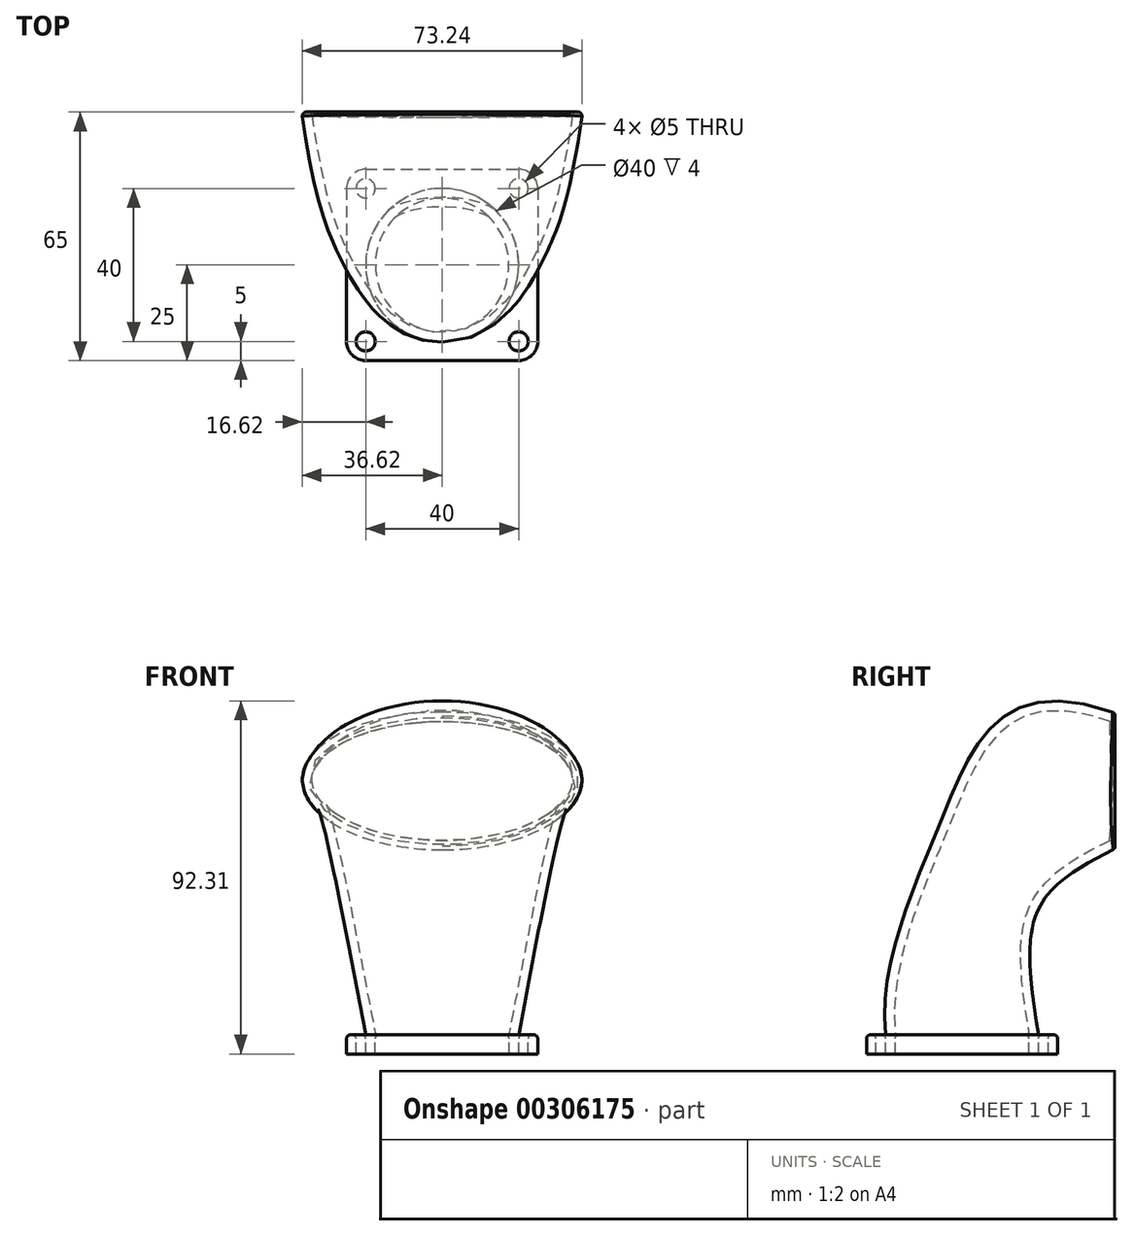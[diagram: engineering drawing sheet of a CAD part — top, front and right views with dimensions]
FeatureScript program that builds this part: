
annotation { "Feature Type Name" : "Feature", "Feature Type Description" : "" }
export const myFeature = defineFeature(function(context is Context, id is Id, definition is map)
    precondition{}
    {
        {
            var Q0;
            Q0=qCreatedBy(makeId("Top.planeOp"),FACE);
            var sketch = newSketch(context, id + "F0", { "sketchPlane" : qUnion([Q0])});
            skCircle(sketch, "E0", {"center": v(0, 0) * mm, "radius": 20 * mm});
            skSolve(sketch);
        }
        {
            var Q0;
            Q0=qCreatedBy(makeId("Front.planeOp"),FACE);
            cPlane(context, id + "F1", {"entities" : qUnion([Q0]), "cplaneType" : CPlaneType.OFFSET, "offset" : 40 * mm, "oppositeDirection" : true, "width" : 150 * mm, "height" : 150 * mm});
        }
        {
            var Q0;
            Q0=qCreatedBy(id+"F1.planeOp",FACE);
            var sketch = newSketch(context, id + "F2", { "sketchPlane" : qUnion([Q0])});
            skEllipse(sketch, "E1", {"center": v(0, 66.4) * mm, "majorRadius": 36.68 * mm, "minorRadius": 17.71 * mm, "majorAxis": v(-1, 0)});
            skSolve(sketch);
        }
        {
            var Q0;
            Q0=qCreatedBy(makeId("Right.planeOp"),FACE);
            var sketch = newSketch(context, id + "F3", { "sketchPlane" : qUnion([Q0])});
            skPoint(sketch, "E2.0", {"position": v(40, 66.4) * mm});
            skLineSegment(sketch, "E3.0", {"start": v(40, 84.11) * mm, "end": v(40, 48.69) * mm});
            skLineSegment(sketch, "E4.0", {"start": v(-20, 0) * mm, "end": v(20, 0) * mm});
            skFitSpline(sketch, "E5", {"points": [v(-20, 0) * mm, v(-5.5, 56.1) * mm, v(40, 84.11) * mm], "startDerivative": vector(-10.12, 108.82) * mm, "endDerivative": vector(186.53, -68.64) * mm});
            skFitSpline(sketch, "E6", {"points": [v(20, 0) * mm, v(20, 32.97) * mm, v(40, 48.69) * mm], "startDerivative": vector(-11.39, 69.47) * mm, "endDerivative": vector(52.77, 26.98) * mm});
            skSolve(sketch);
        }
        {
            var Q0;
            Q0=makeQuery(id+"F0.imprint","IMPRINT",FACE,{"disambiguationData":[TD([[makeQuery(id+"F0.imprint","IMPRINT",EDGE,{"derivedFrom":sQuery(id+"F0.wireOp",EDGE,"E0")}),1.0]])]});
            var Q1;
            Q1=makeQuery(id+"F2.imprint","IMPRINT",FACE,{"disambiguationData":[TD([[makeQuery(id+"F2.imprint","IMPRINT",EDGE,{"derivedFrom":sQuery(id+"F2.wireOp",EDGE,"E1")}),1.0]])]});
            var Q2;
            Q2=sQuery(id+"F3.wireOp",EDGE,"E5");
            var Q3;
            Q3=sQuery(id+"F3.wireOp",EDGE,"E6");
            loft(context, id + "F4", {"addGuides" : true, "sheetProfilesArray" : [{ "sheetProfileEntities" : qUnion([Q0]) }, { "sheetProfileEntities" : qUnion([Q1]) }], "guidesArray" : [{ "guideEntities" : qUnion([Q2]), "guideDerivativeType" : LoftGuideDerivativeType.DEFAULT, "guideDerivativeMagnitude" : 1 }, { "guideEntities" : qUnion([Q3]), "guideDerivativeType" : LoftGuideDerivativeType.DEFAULT, "guideDerivativeMagnitude" : 1 }]});
        }
        {
            var Q0;
            Q0=makeQuery(id+"F4.opLoft","CAP_FACE",FACE,{"disambiguationData":[OSD([makeQuery(id+"F2.imprint","IMPRINT",FACE,{"disambiguationData":[TD([[makeQuery(id+"F2.imprint","IMPRINT",EDGE,{"derivedFrom":sQuery(id+"F2.wireOp",EDGE,"E1")}),1.0]])]})])],"isStart":true});
            var Q1;
            Q1=makeQuery(id+"F4.opLoft","CAP_FACE",FACE,{"disambiguationData":[OSD([makeQuery(id+"F0.imprint","IMPRINT",FACE,{"disambiguationData":[TD([[makeQuery(id+"F0.imprint","IMPRINT",EDGE,{"derivedFrom":sQuery(id+"F0.wireOp",EDGE,"E0")}),1.0]])]})])],"isStart":true});
            shell(context, id + "F5", {"entities" : qUnion([Q0, Q1]), "thickness" : 2.5 * mm});
        }
        {
            var Q0;
            Q0=makeQuery(id+"F0.imprint","IMPRINT",FACE,{"disambiguationData":[TD([[makeQuery(id+"F0.imprint","IMPRINT",EDGE,{"derivedFrom":sQuery(id+"F0.wireOp",EDGE,"E0")}),1.0]])]});
            var sketch = newSketch(context, id + "F6", { "sketchPlane" : qUnion([Q0])});
            skLineSegment(sketch, "E7.bottom", {"start": v(-20, 25) * mm, "end": v(20, 25) * mm});
            skLineSegment(sketch, "E7.top", {"start": v(-20, -25) * mm, "end": v(20, -25) * mm});
            skLineSegment(sketch, "E7.left", {"start": v(-25, 20) * mm, "end": v(-25, -20) * mm});
            skLineSegment(sketch, "E7.right", {"start": v(25, 20) * mm, "end": v(25, -20) * mm});
            skPoint(sketch, "E7.middle", {"position": v(0, 0) * mm});
            skPoint(sketch, "E8.visualSharp", {"position": v(25, -25) * mm});
            skArc(sketch, "E8.filletArc", {"start": v(20, -25) * mm, "mid": v(23.54, -23.54) * mm, "end": v(25, -20) * mm});
            skPoint(sketch, "E9.visualSharp", {"position": v(25, 25) * mm});
            skArc(sketch, "E9.filletArc", {"start": v(25, 20) * mm, "mid": v(23.54, 23.54) * mm, "end": v(20, 25) * mm});
            skPoint(sketch, "E10.visualSharp", {"position": v(-25, 25) * mm});
            skArc(sketch, "E10.filletArc", {"start": v(-20, 25) * mm, "mid": v(-23.54, 23.54) * mm, "end": v(-25, 20) * mm});
            skPoint(sketch, "E11.visualSharp", {"position": v(-25, -25) * mm});
            skArc(sketch, "E11.filletArc", {"start": v(-25, -20) * mm, "mid": v(-23.54, -23.54) * mm, "end": v(-20, -25) * mm});
            skCircle(sketch, "E12", {"center": v(20, 20) * mm, "radius": 2.5 * mm});
            skCircle(sketch, "E13", {"center": v(-20, 20) * mm, "radius": 2.5 * mm});
            skCircle(sketch, "E14", {"center": v(-20, -20) * mm, "radius": 2.5 * mm});
            skCircle(sketch, "E15", {"center": v(20, -20) * mm, "radius": 2.5 * mm});
            skFitSpline(sketch, "E16.0", {"points": [v(-3.84, -17.1) * mm, v(-2.13, -17.39) * mm, v(-0.4, -17.51) * mm, v(1.3, -17.47) * mm, v(3, -17.26) * mm, v(4.7, -16.88) * mm, v(6.31, -16.34) * mm, v(7.61, -15.76) * mm, v(8.62, -15.22) * mm, v(9.61, -14.62) * mm, v(10.78, -13.8) * mm, v(12.07, -12.67) * mm, v(13.05, -11.64) * mm, v(13.78, -10.74) * mm, v(14.46, -9.82) * mm, v(15.22, -8.61) * mm, v(15.86, -7.34) * mm, v(16.3, -6.28) * mm, v(16.68, -5.19) * mm, v(17.06, -3.81) * mm, v(17.35, -2.13) * mm, v(17.46, -0.7) * mm, v(17.46, 0.45) * mm, v(17.38, 2.17) * mm, v(17.09, 3.85) * mm, v(16.6, 5.5) * mm, v(16.21, 6.59) * mm, v(15.64, 7.9) * mm, v(14.8, 9.38) * mm, v(13.98, 10.55) * mm, v(13.25, 11.45) * mm, v(12.48, 12.3) * mm, v(11.44, 13.28) * mm, v(10.1, 14.32) * mm, v(8.63, 15.25) * mm, v(7.1, 16.01) * mm, v(5.76, 16.52) * mm, v(4.67, 16.85) * mm, v(3.83, 17.06) * mm, v(2.98, 17.22) * mm, v(1.85, 17.39) * mm, v(0.43, 17.49) * mm, v(-1.28, 17.45) * mm, v(-3, 17.24) * mm, v(-4.7, 16.86) * mm, v(-6.32, 16.33) * mm, v(-7.62, 15.76) * mm, v(-8.63, 15.22) * mm, v(-9.63, 14.63) * mm, v(-10.8, 13.8) * mm, v(-12.09, 12.7) * mm, v(-13.07, 11.66) * mm, v(-13.8, 10.76) * mm, v(-14.49, 9.84) * mm, v(-15.24, 8.63) * mm, v(-15.88, 7.36) * mm, v(-16.31, 6.3) * mm, v(-16.7, 5.2) * mm, v(-17.07, 3.83) * mm, v(-17.36, 2.15) * mm, v(-17.46, 0.72) * mm, v(-17.46, -0.43) * mm, v(-17.37, -2.15) * mm, v(-17.08, -3.83) * mm, v(-16.58, -5.48) * mm, v(-16.2, -6.57) * mm, v(-15.61, -7.87) * mm, v(-14.78, -9.36) * mm, v(-13.96, -10.53) * mm, v(-13.22, -11.42) * mm, v(-12.46, -12.27) * mm, v(-11.43, -13.26) * mm, v(-10.3, -14.14) * mm, v(-9.35, -14.78) * mm, v(-8.36, -15.37) * mm, v(-7.09, -16.01) * mm, v(-5.5, -16.63) * mm, v(-3.84, -17.1) * mm, v(-2.13, -17.39) * mm, v(-0.4, -17.51) * mm, v(-3.84, -17.1) * mm]});
            skSolve(sketch);
        }
        {
            var Q0;
            Q0=makeQuery(id+"F6.imprint","IMPRINT",FACE,{"disambiguationData":[TD([[makeQuery(id+"F6.imprint","IMPRINT",EDGE,{"derivedFrom":sQuery(id+"F6.wireOp",EDGE,"E7.bottom")}),-1.0]])]});
            var Q1;
            Q1=makeQuery(id+"F6.imprint","IMPRINT",FACE,{"disambiguationData":[TD([[makeQuery(id+"F6.imprint","IMPRINT",EDGE,{"derivedFrom":sQuery(id+"F6.wireOp",EDGE,"E16.0")}),-1.0]])]});
            extrude(context, id + "F7", {"entities" : qUnion([Q0, Q1]), "operationType" : NewBodyOperationType.ADD, "oppositeDirection" : true, "depth" : 5 * mm});
        }
        {
            var Q0;
            Q0=makeQuery(id+"F7.opExtrude","CAP_FACE",FACE,{"disambiguationData":[OSD([sQuery(id+"F6.wireOp",EDGE,"E7.bottom"),sQuery(id+"F6.wireOp",EDGE,"E7.top"),sQuery(id+"F6.wireOp",EDGE,"E7.left"),sQuery(id+"F6.wireOp",EDGE,"E7.right"),sQuery(id+"F6.wireOp",EDGE,"E8.filletArc"),sQuery(id+"F6.wireOp",EDGE,"E9.filletArc"),sQuery(id+"F6.wireOp",EDGE,"E10.filletArc"),sQuery(id+"F6.wireOp",EDGE,"E11.filletArc"),sQuery(id+"F6.wireOp",EDGE,"E12"),sQuery(id+"F6.wireOp",EDGE,"E13"),sQuery(id+"F6.wireOp",EDGE,"E14"),sQuery(id+"F6.wireOp",EDGE,"E15"),sQuery(id+"F6.wireOp",EDGE,"E16.0")])],"isStart":true});
            fillet(context, id + "F8", {"entities" : qUnion([Q0]), "radius" : 1 * mm, "tangentPropagation" : true, "allowEdgeOverflow" : false});
        }
        {
            var Q0;
            Q0=makeQuery(id+"F5.opShell","OFFSET_EDGE",EDGE,{"disambiguationData":[OSD([sQuery(id+"F2.wireOp",EDGE,"E1"),sQuery(id+"F3.wireOp",EDGE,"E5"),sQuery(id+"F3.wireOp",EDGE,"E6")])]});
            var Q1;
            Q1=makeQuery(id+"F4.opLoft","MID_CAP_EDGE",EDGE,{"disambiguationData":[OSD([sQuery(id+"F2.wireOp",EDGE,"E1"),sQuery(id+"F3.wireOp",EDGE,"E5"),sQuery(id+"F3.wireOp",EDGE,"E6")]),OD(1.0)],"capPos":1.0});
            var Q2;
            Q2=makeQuery(id+"F4.opLoft","MID_CAP_EDGE",EDGE,{"disambiguationData":[OSD([sQuery(id+"F2.wireOp",EDGE,"E1"),sQuery(id+"F3.wireOp",EDGE,"E5"),sQuery(id+"F3.wireOp",EDGE,"E6")]),OD(0.0)],"capPos":1.0});
            fillet(context, id + "F9", {"entities" : qUnion([Q0, Q1, Q2]), "radius" : 1 * mm, "tangentPropagation" : true, "allowEdgeOverflow" : false});
        }
    });
